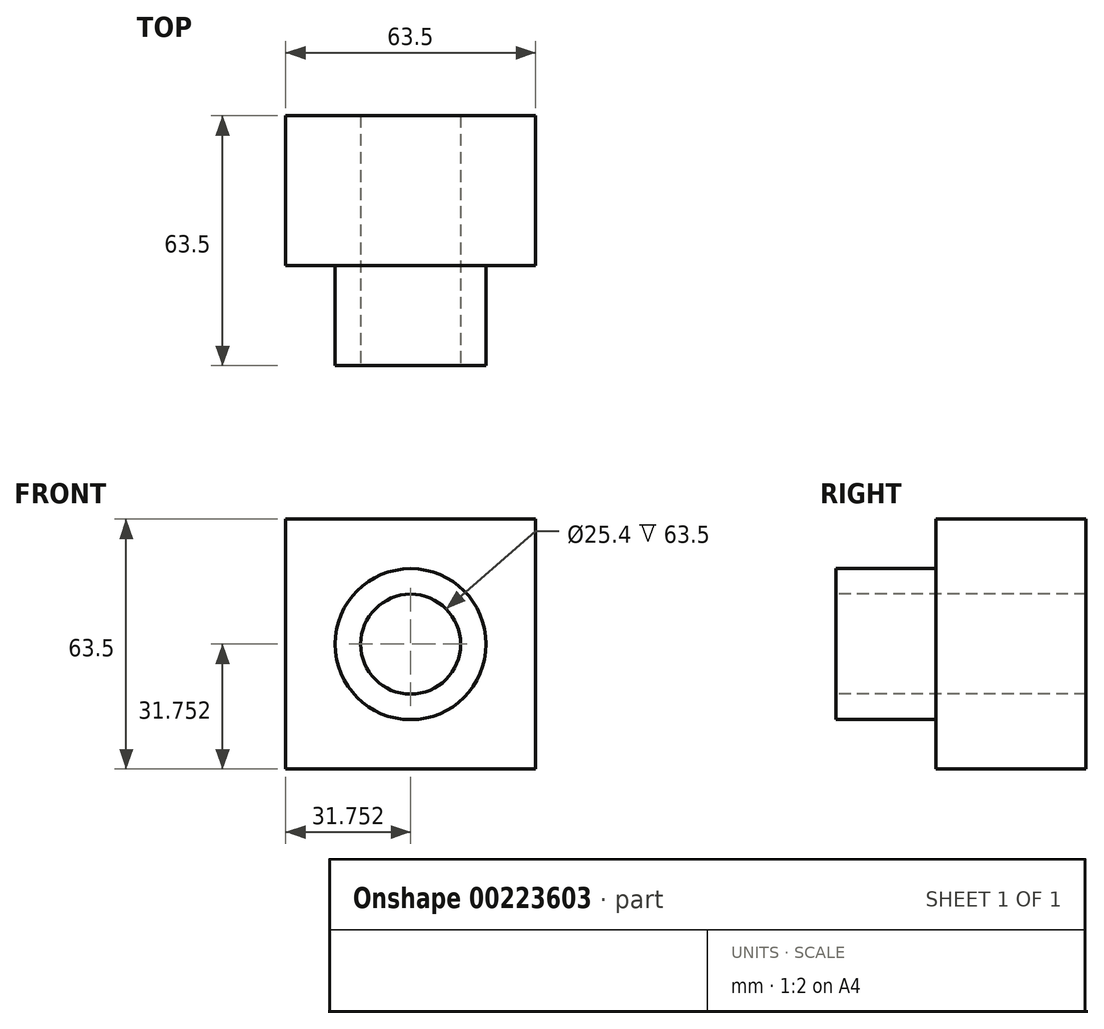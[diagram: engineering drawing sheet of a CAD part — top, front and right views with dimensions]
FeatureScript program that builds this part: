
annotation { "Feature Type Name" : "Feature", "Feature Type Description" : "" }
export const myFeature = defineFeature(function(context is Context, id is Id, definition is map)
    precondition{}
    {
        {
            var Q0;
            Q0=qCreatedBy(makeId("Front.planeOp"),FACE);
            var sketch = newSketch(context, id + "F0", { "sketchPlane" : qUnion([Q0])});
            skLineSegment(sketch, "E0.bottom", {"start": v(-27.58, 30.2) * mm, "end": v(35.92, 30.2) * mm});
            skLineSegment(sketch, "E0.top", {"start": v(-27.58, -33.3) * mm, "end": v(35.92, -33.3) * mm});
            skLineSegment(sketch, "E0.left", {"start": v(-27.58, 30.2) * mm, "end": v(-27.58, -33.3) * mm});
            skLineSegment(sketch, "E0.right", {"start": v(35.92, 30.2) * mm, "end": v(35.92, -33.3) * mm});
            skSolve(sketch);
        }
        {
            var Q0;
            Q0=makeQuery(id+"F0.imprint","IMPRINT",FACE,{"disambiguationData":[TD([[makeQuery(id+"F0.imprint","IMPRINT",EDGE,{"derivedFrom":sQuery(id+"F0.wireOp",EDGE,"E0.bottom")}),-1.0]])]});
            extrude(context, id + "F1", {"entities" : qUnion([Q0]), "depth" : 63.5 * mm});
        }
        {
            var Q0;
            Q0=makeQuery(id+"F1.opExtrude","CAP_FACE",FACE,{"disambiguationData":[OSD([sQuery(id+"F0.wireOp",EDGE,"E0.bottom"),sQuery(id+"F0.wireOp",EDGE,"E0.top"),sQuery(id+"F0.wireOp",EDGE,"E0.left"),sQuery(id+"F0.wireOp",EDGE,"E0.right")])],"isStart":false});
            var sketch = newSketch(context, id + "F2", { "sketchPlane" : qUnion([Q0])});
            skCircle(sketch, "E1", {"center": v(4.17, -1.55) * mm, "radius": 19.17 * mm});
            skSolve(sketch);
        }
        {
            var Q0;
            Q0=makeQuery(id+"F2.imprint","IMPRINT",FACE,{"disambiguationData":[TD([[makeQuery(id+"F2.imprint","IMPRINT",EDGE,{"derivedFrom":sQuery(id+"F2.wireOp",EDGE,"E1")}),-1.0]])]});
            extrude(context, id + "F3", {"entities" : qUnion([Q0]), "operationType" : NewBodyOperationType.REMOVE, "oppositeDirection" : true, "depth" : 25.4 * mm});
        }
        {
            var Q0;
            Q0=makeQuery(id+"F1.opExtrude","CAP_FACE",FACE,{"disambiguationData":[OSD([sQuery(id+"F0.wireOp",EDGE,"E0.bottom"),sQuery(id+"F0.wireOp",EDGE,"E0.top"),sQuery(id+"F0.wireOp",EDGE,"E0.left"),sQuery(id+"F0.wireOp",EDGE,"E0.right")])],"isStart":false});
            var sketch = newSketch(context, id + "F4", { "sketchPlane" : qUnion([Q0])});
            skCircle(sketch, "E2", {"center": v(4.17, -1.55) * mm, "radius": 12.7 * mm});
            skSolve(sketch);
        }
        {
            var Q0;
            Q0=makeQuery(id+"F4.imprint","IMPRINT",FACE,{"disambiguationData":[TD([[makeQuery(id+"F4.imprint","IMPRINT",EDGE,{"derivedFrom":sQuery(id+"F4.wireOp",EDGE,"E2")}),1.0]])]});
            extrude(context, id + "F5", {"entities" : qUnion([Q0]), "operationType" : NewBodyOperationType.REMOVE, "oppositeDirection" : true, "depth" : 63.75 * mm});
        }
    });
